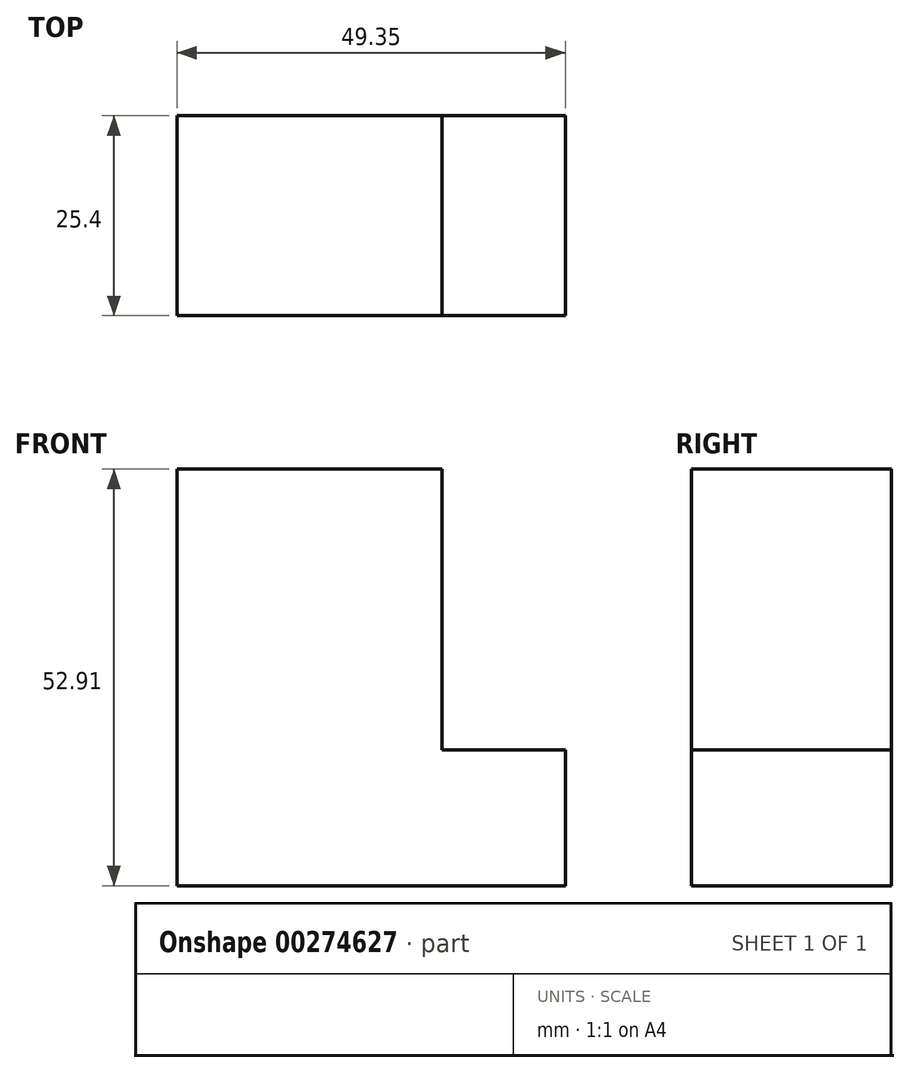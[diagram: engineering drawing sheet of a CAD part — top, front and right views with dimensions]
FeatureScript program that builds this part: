
annotation { "Feature Type Name" : "Feature", "Feature Type Description" : "" }
export const myFeature = defineFeature(function(context is Context, id is Id, definition is map)
    precondition{}
    {
        {
            var Q0;
            Q0=qCreatedBy(makeId("Front.planeOp"),FACE);
            var sketch = newSketch(context, id + "F0", { "sketchPlane" : qUnion([Q0])});
            skLineSegment(sketch, "E0", {"start": v(0, 0) * mm, "end": v(-49.35, 0) * mm});
            skLineSegment(sketch, "E1", {"start": v(-49.35, 0) * mm, "end": v(-49.35, 52.91) * mm});
            skLineSegment(sketch, "E2", {"start": v(-49.35, 52.91) * mm, "end": v(-15.69, 52.91) * mm});
            skLineSegment(sketch, "E3", {"start": v(-15.69, 52.91) * mm, "end": v(-15.69, 17.26) * mm});
            skLineSegment(sketch, "E4", {"start": v(-15.69, 17.26) * mm, "end": v(0, 17.26) * mm});
            skLineSegment(sketch, "E5", {"start": v(0, 17.26) * mm, "end": v(0, 0) * mm});
            skSolve(sketch);
        }
        {
            var Q0;
            Q0 = qSketchRegion(id + "F0", true);
            extrude(context, id + "F1", {"entities" : qUnion([Q0]), "depth" : 25.4 * mm});
        }
    });
